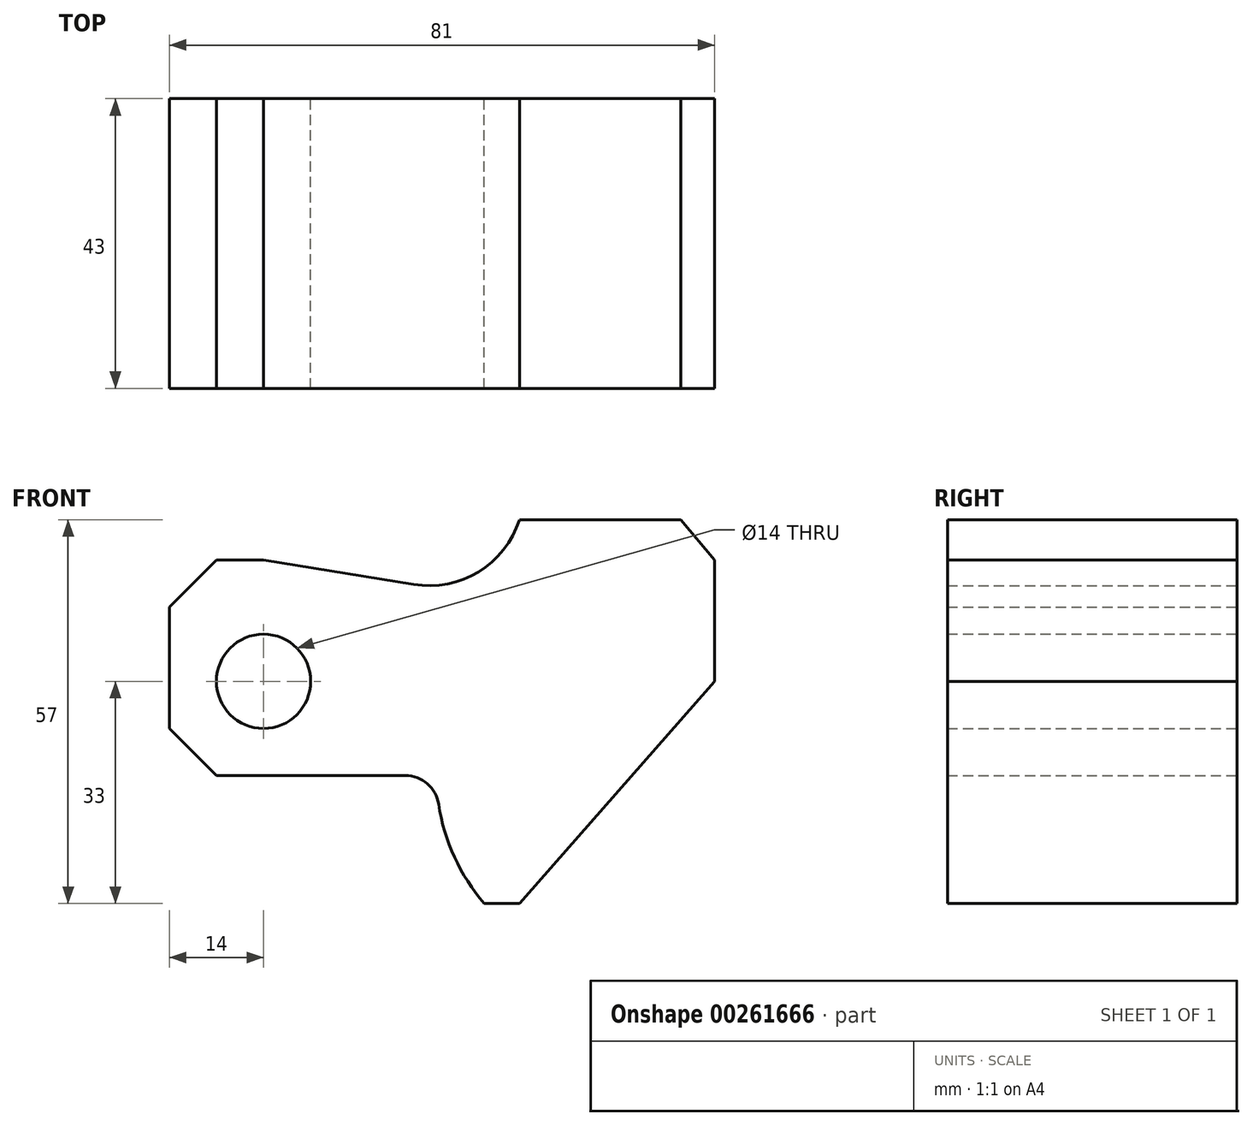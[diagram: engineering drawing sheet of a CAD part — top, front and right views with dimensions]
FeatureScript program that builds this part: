
annotation { "Feature Type Name" : "Feature", "Feature Type Description" : "" }
export const myFeature = defineFeature(function(context is Context, id is Id, definition is map)
    precondition{}
    {
        {
            var Q0;
            Q0=qCreatedBy(makeId("Front.planeOp"),FACE);
            var sketch = newSketch(context, id + "F0", { "sketchPlane" : qUnion([Q0])});
            skLineSegment(sketch, "E0.bottom", {"start": v(11.5, 28.5) * mm, "end": v(35.5, 28.5) * mm});
            skLineSegment(sketch, "E0.left", {"start": v(-40.5, 15.5) * mm, "end": v(-40.5, -2.5) * mm});
            skLineSegment(sketch, "E0.right", {"start": v(40.5, 22.5) * mm, "end": v(40.5, 4.5) * mm});
            skPoint(sketch, "E0.middle", {"position": v(0, 0) * mm});
            skLineSegment(sketch, "E1", {"start": v(40.5, 4.5) * mm, "end": v(11.5, -28.5) * mm});
            skLineSegment(sketch, "E2", {"start": v(35.5, 28.5) * mm, "end": v(40.5, 22.5) * mm});
            skCircle(sketch, "E3", {"center": v(-26.5, 4.5) * mm, "radius": 7 * mm});
            skLineSegment(sketch, "E4.top", {"start": v(-33.5, -9.5) * mm, "end": v(-5.43, -9.5) * mm});
            skPoint(sketch, "E5.orphan", {"position": v(-40.5, 28.5) * mm});
            skPoint(sketch, "E6.orphan", {"position": v(40.5, 28.5) * mm});
            skPoint(sketch, "E7.orphan", {"position": v(40.5, -28.5) * mm});
            skPoint(sketch, "E0.top.start.orphan", {"position": v(-40.5, -28.5) * mm});
            skArc(sketch, "E8", {"start": v(-0.49, -13.76) * mm, "mid": v(1.85, -21.62) * mm, "end": v(6.29, -28.5) * mm});
            skLineSegment(sketch, "E9", {"start": v(11.5, -28.5) * mm, "end": v(6.29, -28.5) * mm});
            skPoint(sketch, "E10.visualSharp", {"position": v(-0.8, -9.5) * mm});
            skArc(sketch, "E10.filletArc", {"start": v(-0.49, -13.76) * mm, "mid": v(-2.17, -10.71) * mm, "end": v(-5.43, -9.5) * mm});
            skLineSegment(sketch, "E11.top", {"start": v(-33.5, 22.5) * mm, "end": v(-26.5, 22.5) * mm});
            skLineSegment(sketch, "E11.left", {"start": v(-40.5, -2.5) * mm, "end": v(-40.5, 15.5) * mm});
            skLineSegment(sketch, "E11.right", {"start": v(40.5, 4.5) * mm, "end": v(40.5, 22.5) * mm});
            skLineSegment(sketch, "E12.top", {"start": v(35.5, 28.5) * mm, "end": v(11.5, 28.5) * mm});
            skLineSegment(sketch, "E12.left", {"start": v(40.5, 11.35) * mm, "end": v(40.5, 22.5) * mm});
            skLineSegment(sketch, "E13", {"start": v(-40.5, 15.5) * mm, "end": v(-33.5, 22.5) * mm});
            skLineSegment(sketch, "E14", {"start": v(-40.5, -2.5) * mm, "end": v(-33.5, -9.5) * mm});
            skLineSegment(sketch, "E15.top", {"start": v(-26.5, 22.5) * mm, "end": v(-33.5, 22.5) * mm});
            skLineSegment(sketch, "E15.right", {"start": v(-40.5, 4.5) * mm, "end": v(-40.5, 15.5) * mm});
            skPoint(sketch, "E16.orphan", {"position": v(-40.5, 22.5) * mm});
            skLineSegment(sketch, "E17", {"start": v(-26.5, 22.5) * mm, "end": v(-3.96, 18.86) * mm});
            skArc(sketch, "E18", {"start": v(-4.22, 18.9) * mm, "mid": v(5.44, 20.75) * mm, "end": v(11.5, 28.5) * mm});
            skPoint(sketch, "E19.end.orphan", {"position": v(11.5, 22.5) * mm});
            skPoint(sketch, "E20.end.orphan", {"position": v(11.5, 23.52) * mm});
            skSolve(sketch);
        }
        {
            var Q0;
            Q0=makeQuery(id+"F0.imprint","IMPRINT",FACE,{"disambiguationData":[TD([[makeQuery(id+"F0.imprint","IMPRINT",EDGE,{"derivedFrom":sQuery(id+"F0.wireOp",EDGE,"E1")}),-1.0]])]});
            extrude(context, id + "F1", {"entities" : qUnion([Q0]), "depth" : 43 * mm});
        }
    });
